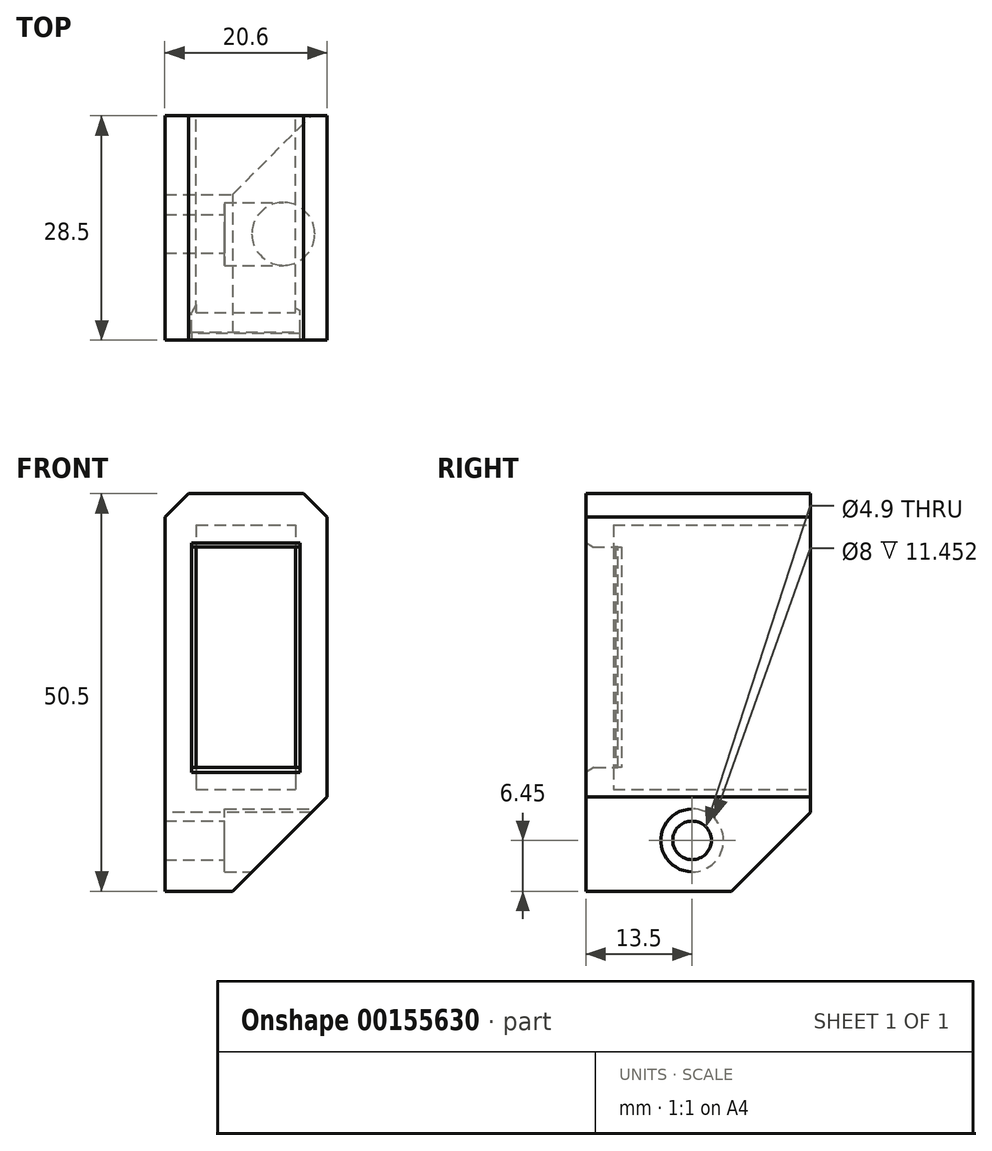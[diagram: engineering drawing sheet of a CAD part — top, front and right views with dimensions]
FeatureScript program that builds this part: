
annotation { "Feature Type Name" : "Feature", "Feature Type Description" : "" }
export const myFeature = defineFeature(function(context is Context, id is Id, definition is map)
    precondition{}
    {
        {
            var Q0;
            Q0=qCreatedBy(makeId("Front.planeOp"),FACE);
            var sketch = newSketch(context, id + "F0", { "sketchPlane" : qUnion([Q0])});
            skLineSegment(sketch, "E0.bottom", {"start": v(-16.36, 27) * mm, "end": v(-3.76, 27) * mm});
            skLineSegment(sketch, "E0.top", {"start": v(-16.36, -6.6) * mm, "end": v(-3.76, -6.6) * mm});
            skLineSegment(sketch, "E0.left", {"start": v(-16.36, 27) * mm, "end": v(-16.36, -6.6) * mm});
            skLineSegment(sketch, "E0.right", {"start": v(-3.76, 27) * mm, "end": v(-3.76, -6.6) * mm});
            skLineSegment(sketch, "E1.0", {"start": v(-20.36, 31) * mm, "end": v(0.24, 31) * mm});
            skLineSegment(sketch, "E1.1", {"start": v(-20.36, 31) * mm, "end": v(-20.36, -10.6) * mm});
            skLineSegment(sketch, "E1.2", {"start": v(-20.36, -10.6) * mm, "end": v(0.24, -10.6) * mm});
            skLineSegment(sketch, "E1.3", {"start": v(0.24, 31) * mm, "end": v(0.24, -10.6) * mm});
            skSolve(sketch);
        }
        {
            var Q0;
            Q0 = qSketchRegion(id + "F0", true);
            extrude(context, id + "F1", {"entities" : qUnion([Q0]), "depth" : 25 * mm});
        }
        {
            var Q0;
            Q0=makeQuery(id+"F1.opExtrude","CAP_FACE",FACE,{"disambiguationData":[OSD([sQuery(id+"F0.wireOp",EDGE,"E0.bottom"),sQuery(id+"F0.wireOp",EDGE,"E0.top"),sQuery(id+"F0.wireOp",EDGE,"E0.left"),sQuery(id+"F0.wireOp",EDGE,"E0.right"),sQuery(id+"F0.wireOp",EDGE,"E1.0"),sQuery(id+"F0.wireOp",EDGE,"E1.1"),sQuery(id+"F0.wireOp",EDGE,"E1.2"),sQuery(id+"F0.wireOp",EDGE,"E1.3")])],"isStart":false});
            var sketch = newSketch(context, id + "F2", { "sketchPlane" : qUnion([Q0])});
            skLineSegment(sketch, "E2.bottom", {"start": v(-16.96, 24.2) * mm, "end": v(-3.16, 24.2) * mm});
            skLineSegment(sketch, "E2.top", {"start": v(-16.96, -3.8) * mm, "end": v(-3.16, -3.8) * mm});
            skLineSegment(sketch, "E2.left", {"start": v(-16.96, 24.2) * mm, "end": v(-16.96, -3.8) * mm});
            skLineSegment(sketch, "E2.right", {"start": v(-3.16, 24.2) * mm, "end": v(-3.16, -3.8) * mm});
            skPoint(sketch, "E2.middle", {"position": v(-10.06, 10.2) * mm});
            skPoint(sketch, "E2.middle.positionSnap0", {"position": v(-10.06, -6.6) * mm});
            skPoint(sketch, "E2.middle.positionSnap1", {"position": v(-16.36, 10.2) * mm});
            skPoint(sketch, "E2.centerSnap0", {"position": v(-10.06, -6.6) * mm});
            skPoint(sketch, "E2.centerSnap1", {"position": v(-16.36, 10.2) * mm});
            skLineSegment(sketch, "E3.bottom", {"start": v(-20.36, 31) * mm, "end": v(0.24, 31) * mm});
            skLineSegment(sketch, "E3.top", {"start": v(-20.36, -10.6) * mm, "end": v(0.24, -10.6) * mm});
            skLineSegment(sketch, "E3.left", {"start": v(-20.36, 31) * mm, "end": v(-20.36, -10.6) * mm});
            skLineSegment(sketch, "E3.right", {"start": v(0.24, 31) * mm, "end": v(0.24, -10.6) * mm});
            skSolve(sketch);
        }
        {
            var Q0;
            Q0 = qSketchRegion(id + "F2", true);
            extrude(context, id + "F3", {"entities" : qUnion([Q0]), "operationType" : NewBodyOperationType.ADD, "depth" : 3.5 * mm});
        }
        {
            var Q0;
            {var subQ0=sQuery(id+"F0.wireOp",EDGE,"E0.left");Q0=makeQuery(id+"F3.boolean.opBoolean","SPLIT",EDGE,{"disambiguationData":[topologyDisambiguationEdgeConnected([makeQuery(id+"F1.opExtrude","CAP_FACE",FACE,{"disambiguationData":[OSD([sQuery(id+"F0.wireOp",EDGE,"E0.bottom"),sQuery(id+"F0.wireOp",EDGE,"E0.top"),subQ0,sQuery(id+"F0.wireOp",EDGE,"E0.right"),sQuery(id+"F0.wireOp",EDGE,"E1.0"),sQuery(id+"F0.wireOp",EDGE,"E1.1"),sQuery(id+"F0.wireOp",EDGE,"E1.2"),sQuery(id+"F0.wireOp",EDGE,"E1.3")])],"isStart":false}),makeQuery(id+"F1.opExtrude","SWEPT_FACE",FACE,{"disambiguationData":[OSD([subQ0])]})])],"derivedFrom":makeQuery(id+"F1.opExtrude","CAP_EDGE",EDGE,{"disambiguationData":[OSD([subQ0])],"isStart":false})});}
            var Q1;
            {var subQ0=sQuery(id+"F0.wireOp",EDGE,"E0.right");Q1=makeQuery(id+"F3.boolean.opBoolean","SPLIT",EDGE,{"disambiguationData":[topologyDisambiguationEdgeConnected([makeQuery(id+"F1.opExtrude","CAP_FACE",FACE,{"disambiguationData":[OSD([sQuery(id+"F0.wireOp",EDGE,"E0.bottom"),sQuery(id+"F0.wireOp",EDGE,"E0.top"),sQuery(id+"F0.wireOp",EDGE,"E0.left"),subQ0,sQuery(id+"F0.wireOp",EDGE,"E1.0"),sQuery(id+"F0.wireOp",EDGE,"E1.1"),sQuery(id+"F0.wireOp",EDGE,"E1.2"),sQuery(id+"F0.wireOp",EDGE,"E1.3")])],"isStart":false}),makeQuery(id+"F1.opExtrude","SWEPT_FACE",FACE,{"disambiguationData":[OSD([subQ0])]})])],"derivedFrom":makeQuery(id+"F1.opExtrude","CAP_EDGE",EDGE,{"disambiguationData":[OSD([subQ0])],"isStart":false})});}
            var Q2;
            Q2=makeQuery(id+"F3.opExtrude","CAP_EDGE",EDGE,{"disambiguationData":[OSD([sQuery(id+"F2.wireOp",EDGE,"E2.top")])],"isStart":false});
            chamfer(context, id + "F4", {"entities" : qUnion([Q0, Q1, Q2]), "chamferType" : ChamferType.OFFSET_ANGLE, "width" : .6 * mm, "oppositeDirection" : true, "angle" : 60 * degree, "tangentPropagation" : true});
        }
        {
            var Q0;
            Q0=makeQuery(id+"F3.boolean.opBoolean","MERGE",FACE,{"derivedFrom":[makeQuery(id+"F1.opExtrude","SWEPT_FACE",FACE,{"disambiguationData":[OSD([sQuery(id+"F0.wireOp",EDGE,"E1.3")])]}),makeQuery(id+"F3.opExtrude","SWEPT_FACE",FACE,{"disambiguationData":[OSD([sQuery(id+"F2.wireOp",EDGE,"E3.right")])]})]});
            var sketch = newSketch(context, id + "F5", { "sketchPlane" : qUnion([Q0])});
            skCircle(sketch, "E4", {"center": v(-15, -13.05) * mm, "radius": 2.45 * mm});
            skLineSegment(sketch, "E5.bottom", {"start": v(-28.5, -10.6) * mm, "end": v(0, -10.6) * mm});
            skLineSegment(sketch, "E5.top", {"start": v(-28.5, -19.5) * mm, "end": v(0, -19.5) * mm});
            skLineSegment(sketch, "E5.left", {"start": v(-28.5, -10.6) * mm, "end": v(-28.5, -19.5) * mm});
            skLineSegment(sketch, "E5.right", {"start": v(0, -10.6) * mm, "end": v(0, -19.5) * mm});
            skSolve(sketch);
        }
        {
            var Q0;
            Q0 = qSketchRegion(id + "F5", true);
            var Q1;
            Q1=makeQuery(id+"F3.boolean.opBoolean","MERGE",FACE,{"derivedFrom":[makeQuery(id+"F1.opExtrude","SWEPT_FACE",FACE,{"disambiguationData":[OSD([sQuery(id+"F0.wireOp",EDGE,"E1.1")])]}),makeQuery(id+"F3.opExtrude","SWEPT_FACE",FACE,{"disambiguationData":[OSD([sQuery(id+"F2.wireOp",EDGE,"E3.left")])]})]});
            extrude(context, id + "F6", {"entities" : qUnion([Q0]), "operationType" : NewBodyOperationType.ADD, "endBound" : BoundingType.UP_TO_SURFACE, "oppositeDirection" : true, "endBoundEntityFace" : qUnion([Q1]), "depth" : 13.25 * mm});
        }
        {
            var Q0;
            Q0=makeQuery(id+"F6.boolean.opBoolean","MERGE",FACE,{"derivedFrom":[makeQuery(id+"F3.boolean.opBoolean","MERGE",FACE,{"derivedFrom":[makeQuery(id+"F1.opExtrude","SWEPT_FACE",FACE,{"disambiguationData":[OSD([sQuery(id+"F0.wireOp",EDGE,"E1.3")])]}),makeQuery(id+"F3.opExtrude","SWEPT_FACE",FACE,{"disambiguationData":[OSD([sQuery(id+"F2.wireOp",EDGE,"E3.right")])]})]}),makeQuery(id+"F6.opExtrude","CAP_FACE",FACE,{"disambiguationData":[OSD([sQuery(id+"F5.wireOp",EDGE,"E5.bottom"),sQuery(id+"F5.wireOp",EDGE,"E5.top"),sQuery(id+"F5.wireOp",EDGE,"E5.left"),sQuery(id+"F5.wireOp",EDGE,"E5.right")])],"isStart":true})]});
            var sketch = newSketch(context, id + "F7", { "sketchPlane" : qUnion([Q0])});
            skCircle(sketch, "E6", {"center": v(-15, -13.05) * mm, "radius": 2.45 * mm});
            skSolve(sketch);
        }
        {
            var Q0;
            Q0 = qSketchRegion(id + "F7", true);
            extrude(context, id + "F8", {"entities" : qUnion([Q0]), "operationType" : NewBodyOperationType.REMOVE, "endBound" : BoundingType.THROUGH_ALL, "oppositeDirection" : true, "depth" : 25 * mm});
        }
        {
            var Q0;
            Q0=makeQuery(id+"F3.boolean.opBoolean","MERGE",EDGE,{"derivedFrom":[makeQuery(id+"F1.opExtrude","SWEPT_EDGE",EDGE,{"disambiguationData":[OSD([sQuery(id+"F0.wireOp",EDGE,"E1.0"),sQuery(id+"F0.wireOp",EDGE,"E1.3")])]}),makeQuery(id+"F3.opExtrude","SWEPT_EDGE",EDGE,{"disambiguationData":[OSD([sQuery(id+"F2.wireOp",EDGE,"E3.bottom"),sQuery(id+"F2.wireOp",EDGE,"E3.right")])]})]});
            var Q1;
            Q1=makeQuery(id+"F3.boolean.opBoolean","MERGE",EDGE,{"derivedFrom":[makeQuery(id+"F1.opExtrude","SWEPT_EDGE",EDGE,{"disambiguationData":[OSD([sQuery(id+"F0.wireOp",EDGE,"E1.0"),sQuery(id+"F0.wireOp",EDGE,"E1.1")])]}),makeQuery(id+"F3.opExtrude","SWEPT_EDGE",EDGE,{"disambiguationData":[OSD([sQuery(id+"F2.wireOp",EDGE,"E3.bottom"),sQuery(id+"F2.wireOp",EDGE,"E3.left")])]})]});
            chamfer(context, id + "F9", {"entities" : qUnion([Q0, Q1]), "width" : 3 * mm, "tangentPropagation" : true});
        }
        {
            var Q0;
            Q0=makeQuery(id+"F6.opExtrude","SWEPT_EDGE",EDGE,{"disambiguationData":[OSD([sQuery(id+"F5.wireOp",EDGE,"E5.top"),sQuery(id+"F5.wireOp",EDGE,"E5.right")])]});
            chamfer(context, id + "F10", {"entities" : qUnion([Q0]), "width" : 10 * mm, "tangentPropagation" : true});
        }
        {
            var Q0;
            Q0=makeQuery(id+"F6.boolean.opBoolean","MERGE",FACE,{"derivedFrom":[makeQuery(id+"F3.boolean.opBoolean","MERGE",FACE,{"derivedFrom":[makeQuery(id+"F1.opExtrude","SWEPT_FACE",FACE,{"disambiguationData":[OSD([sQuery(id+"F0.wireOp",EDGE,"E1.3")])]}),makeQuery(id+"F3.opExtrude","SWEPT_FACE",FACE,{"disambiguationData":[OSD([sQuery(id+"F2.wireOp",EDGE,"E3.right")])]})]}),makeQuery(id+"F6.opExtrude","CAP_FACE",FACE,{"disambiguationData":[OSD([sQuery(id+"F5.wireOp",EDGE,"E5.bottom"),sQuery(id+"F5.wireOp",EDGE,"E5.top"),sQuery(id+"F5.wireOp",EDGE,"E5.left"),sQuery(id+"F5.wireOp",EDGE,"E5.right")])],"isStart":true})]});
            var sketch = newSketch(context, id + "F11", { "sketchPlane" : qUnion([Q0])});
            skCircle(sketch, "E7", {"center": v(-15, -13.05) * mm, "radius": 4 * mm});
            skSolve(sketch);
        }
        {
            var Q0;
            Q0 = qSketchRegion(id + "F11", true);
            extrude(context, id + "F12", {"entities" : qUnion([Q0]), "operationType" : NewBodyOperationType.REMOVE, "oppositeDirection" : true, "depth" : 13 * mm});
        }
        {
            var Q0;
            Q0=makeQuery(id+"F6.opExtrude","CAP_EDGE",EDGE,{"disambiguationData":[OSD([sQuery(id+"F5.wireOp",EDGE,"E5.top")])],"isStart":true});
            chamfer(context, id + "F13", {"entities" : qUnion([Q0]), "width" : 12 * mm, "tangentPropagation" : true});
        }
        {
            var Q0;
            Q0=makeQuery(id+"F3.opExtrude","CAP_EDGE",EDGE,{"disambiguationData":[OSD([sQuery(id+"F2.wireOp",EDGE,"E2.bottom")])],"isStart":false});
            chamfer(context, id + "F14", {"entities" : qUnion([Q0]), "chamferType" : ChamferType.OFFSET_ANGLE, "width" : .5 * mm, "oppositeDirection" : false, "angle" : 60 * degree, "tangentPropagation" : true});
        }
    });
